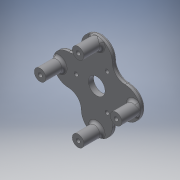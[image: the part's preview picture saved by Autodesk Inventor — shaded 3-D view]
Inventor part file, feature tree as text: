
AUTODESK INVENTOR PART (.ipt)
format: ipt  version: 2019.4 (Build 234330000, 330)  size: 355,840 bytes
history: native  units: mm
features: sketch x7, extrude x5, fillet x4, pattern_circular x3, hole x2
ambient origin geometry x8: Origin, YZ Plane, XZ Plane, XY Plane, X Axis, Y Axis, Z Axis, Center Point
bodies: Solid1 (feature_tree)
feature tree (21):
  extrude  "Extrusion1"  Depth=68.0mm
  extrude  "Extrusion2"  Depth=29.5mm
  hole  "Hole2"  [1 undecoded]
  extrude  "Extrusion3"  Depth=3.0mm
  pattern_circular  "Circular Pattern2"  Count=8 Angle=360.0deg
  fillet  "Fillet1"  Radius=32.0mm
  extrude  "Extrusion4"  Depth=30.0mm TaperAngle=360.0deg
  pattern_circular  "Circular Pattern3"  [2 undecoded]
  fillet  "Fillet3"  Radius=3.0mm
  fillet  "Fillet4"  Radius=40.0mm
  sketch  "Sketch2"  dims[d3=7.0mm d4=29.5mm]
  extrude  "Extrusion5"  Depth=0.4mm
  hole  "Hole5"  [1 undecoded]
  fillet  "Fillet6"  Radius=9.0mm
  pattern_circular  "Circular Pattern5"  [2 undecoded]
  sketch  "Sketch1"  dims[d0=4.0mm d1=0.0mm d2=68.0mm]
  sketch  "Sketch3"  dims[d15=13.0mm d16=3.0mm d17=0.0mm]
  sketch  "Sketch4"  dims[d18=19.0mm d19=3.0mm d20=80.0mm d22=360.0deg d24=32.0mm]
  sketch  "Sketch5"  dims[d25=3.0mm d26=30.0mm d28=360.0deg]
  sketch  "Sketch6"  dims[d30=3.1mm d31=6.0mm d32=6.5mm d33=2.0mm d34=90.0deg d35=10.0mm d36=0.0mm]
  sketch  "Sketch9"  dims[d37=12.0mm d38=12.0mm d39=3.0mm d40=0.0mm d41=40.0mm d42=360.0deg d44=10.0mm d45=12.0mm d46=9.0mm d47=14.5mm d48=0.0mm d50=40.0mm d51=360.0deg d53=2.0mm d54=2.0mm d55=3.0mm d56=0.0mm d75=3.25mm d76=6.0mm d77=6.5mm d78=2.0mm d79=90.0deg d80=15.0mm d81=0.0mm d82=0.4mm d83=40.0mm d84=360.0deg d5=1.0mm d6=1.0mm d7=1.0mm d8=0.15mm d9=0.25mm d10=0.375mm d11=14.3117mm d12=0.75mm d13=20.594885mm d14=0.0625mm]
note: 6 required parameter values undecoded (feature->parameter linkage not recoverable at this tier; creation-order binding heuristic only, values carry confidence <= 0.55)
